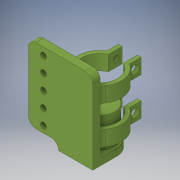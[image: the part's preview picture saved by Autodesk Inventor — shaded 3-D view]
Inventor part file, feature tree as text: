
AUTODESK INVENTOR PART (.ipt)
format: ipt  version: 2018 (Build 220112000, 112)  size: 290,304 bytes
history: native  units: in
note: dims shown in document units (in); Inventor stores cm internally (conversion verified against a paired STEP export)
features: extrude x8, sketch x8, fillet x4, plane x2, pattern_linear x1
ambient origin geometry x8: Origin, YZ Plane, XZ Plane, XY Plane, X Axis, Y Axis, Z Axis, Center Point
bodies: Solid1 (feature_tree)
feature tree (23):
  extrude  "Extrusion1"  Depth=1.0in TaperAngle=0.0deg
  plane  "Work Plane1"
  extrude  "Extrusion2"  Depth=0.5in
  extrude  "Extrusion3"  Depth=0.0984in
  extrude  "Extrusion4"  Depth=0.0787in TaperAngle=0.0deg
  plane  "Work Plane2"
  extrude  "Extrusion5"  Depth=0.25in TaperAngle=0.0deg
  pattern_linear  "Rectangular Pattern1"  Spacing1=0.0625in  [1 undecoded]
  extrude  "Extrusion6"  Depth=1.125in
  extrude  "Extrusion7"  Depth=0.25in
  fillet  "Fillet1"  Radius=2.471in
  extrude  "Extrusion8"  [1 undecoded]
  fillet  "Fillet2"  Radius=0.6729in
  fillet  "Fillet3"  Radius=0.7573in
  fillet  "Fillet4"  Radius=0.1875in
  sketch  "Sketch1"  dims[d0=1.0in d1=1.0in d2=0.0in]
  sketch  "Sketch3"  dims[d3=0.5in d8=0.0945in]
  sketch  "Sketch4"  dims[d9=0.1969in d10=0.0984in]
  sketch  "Sketch5"  dims[d11=0.0945in d12=0.0787in d13=0.0in]
  sketch  "Sketch6"  dims[d14=0.25in d15=0.25in d16=0.0in]
  sketch  "Sketch7"  dims[d17=1.125in]
  sketch  "Sketch8"  dims[d18=0.5625in]
  sketch  "Sketch9"  dims[d19=0.5625in d20=0.0625in d21=1.125in d22=0.25in d23=2.471in d24=0.0in d25=-0.75in d26=1.19in d27=0.125in d28=0.375in d29=1.0in d30=0.125in d31=0.6729in d32=0.7573in d33=0.1875in d34=0.1856in d35=0.3106in d36=0.425in d37=0.55in d38=0.5in d39=0.0in d40=0.7874in d42=1.25in d43=0.194in d44=0.194in d45=0.25in d46=0.25in d47=0.2in d48=0.2in d49=0.5in d50=0.0in d51=0.274in d52=0.274in d53=0.5in d54=0.0in d55=0.2in d56=0.1935in d57=0.5in d59=0.5in d60=0.5in d61=0.5in d64=0.1935in d65=0.1935in d66=0.1935in d67=0.1935in d71=0.25in d72=0.0in d73=2.125in d74=0.5394in d75=0.5in d76=0.25in d77=0.5in d78=0.5in d79=0.5in d80=0.5in d81=0.25in d82=0.25in d83=0.25in]
note: 2 required parameter values undecoded (feature->parameter linkage not recoverable at this tier; creation-order binding heuristic only, values carry confidence <= 0.55)
